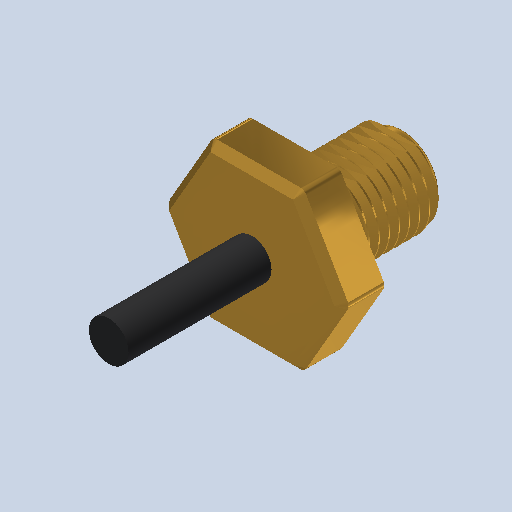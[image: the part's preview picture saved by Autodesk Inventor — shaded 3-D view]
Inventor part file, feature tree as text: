
AUTODESK INVENTOR PART (.ipt)
format: ipt  version: 2024.2 (Build 282272000, 272)  size: 485,376 bytes
history: native  units: mm
features: extrude x6, fillet x3, sketch x3, helix x1, chamfer x1, projected_geometry x1
ambient origin geometry x8: Origin, YZ Plane, XZ Plane, XY Plane, X Axis, Y Axis, Z Axis, Center Point
bodies: Solid1 (feature_tree), Solid2 (feature_tree), Solid3 (feature_tree)
feature tree (15):
  helix  "Coil1"  [1 undecoded]
  extrude  "Extrusion1"  Depth=2.63525mm
  extrude  "Extrusion2"  Depth=0.70612mm
  fillet  "Fillet1"  Radius=10.0mm
  fillet  "Fillet2"  Radius=5.0mm
  extrude  "Extrusion3"  Depth=2.0mm
  extrude  "Extrusion5"  Depth=2.0mm
  extrude  "Extrusion6"  Depth=2.0mm
  extrude  "Extrusion7"  Depth=2.0mm
  fillet  "Fillet3"  Radius=7.6mm
  chamfer  "Chamfer2"  Distance=0.35mm
  projected_geometry  "Projected Loop1"
  sketch  "Sketch6"  dims[d13=2.25mm d14=0.70612mm]
  sketch  "Sketch8"  dims[d15=8.0mm d16=10.0mm d17=0.0mm d18=90.0deg d19=90.0deg d20=0.0mm d21=0.0mm d24=10.0mm d25=0.0mm d26=5.0mm d27=8.0mm d28=2.0mm d29=0.75mm d30=1.27mm d31=7.6mm d32=0.0mm d33=0.35mm d34=0.6mm d41=3.0mm d42=0.0mm d56=1.27mm d57=0.0mm d64=6.4mm d65=5.85mm d66=10.0mm d67=0.0mm d74=11.0mm d75=10.0mm d76=0.0mm d77=0.5mm d78=0.5mm d79=2.0mm d80=45.0deg]
  sketch  "Sketch1"  dims[d9=3.09372mm d11=2.63525mm]
note: 1 required parameter value undecoded (feature->parameter linkage not recoverable at this tier; creation-order binding heuristic only, values carry confidence <= 0.55)
